# Revit family: Elevator_10913
name_source: partatom
category: Generic Models
revit_build: Autodesk Revit 2016 (Build: 20150714_1515(x64)
units: mm (PartAtom-declared; Revit-internal decimal feet)

## family parameters
Always vertical = Yes
Can host rebar = No
Cut with Voids When Loaded = No
Host = Wall
Part Type = Normal
Room Calculation Point = No
Round Connector Dimension = Use Diameter
Shared = No

## types (8) — shared parameters
Car Offset at Frame_Right = 0.14 m
Car Wall Thickness = 0.03 m
Dimension 03 = 0.03 m
Dimension 04 = 0.11 m
Dimension B = 1.05 m
Dimension L = 0.17 m
Door Thickness = 0.03 m
Frame Offset_Inside = 0.03 m
Frame Width = 0.05 m
Left Lobby Door Offset = 0.03 m
Weight Capacity Type Information = 1=2000 / 2=2500 / 3=3000 / 4=3500 / 5=4000 / 6=4500 / 7=5000 / 8=6000 / 9=10,000 / 10=12,000
_Elevator Door Height = 2.13 m
_Elevator Pit Depth = 1.22 m

## per-type parameters (varying)
- Service / Hospital_4000: CDI Car Inside=2.26 m; CWI Car Inside=1.73 m; CWI Car Inside Left=1.04 m; CWI Car Inside Right=0.69 m; CWI Car Inside_Half=0.86 m; Car Offset From Wall=0.27 m; Car Offset at Frame_Left=0.1 m; Centerline of Car Opening=1.61 m; Centerline of Opening=1.61 m; Clear Opening=1.22 m; Clear Opening_Half=0.61 m; Dimension 02=0.14 m; Dimension F=1.39 m; Dimension K=1.25 m; HD CL Hoistway and Pit=2.79 m; HW Clear Hoistway and Pit=2.54 m; Head and Sill_Left of Center=1.37 m; Head and Sill_Right of Center=0.71 m; Horizontal Location of Left Door=1.64 m; Horizontal Location of Right Door=1.59 m; Left Elevator Door Offset=0.27 m; Left Elevator Door Width=0.69 m; Rail Layout 01=Yes; Rail Layout 02=No; Right Elevator Door Offset=0.23 m; Right Elevator Door Width=0.69 m; Right Lobby Door Offset=0.07 m; Sill Width=0.11 m; WC=4000; Weight Capacity Type=5; _Elevator Car Inside Width Dimension=1.73 m; _Elevator Clear Hoistway Depth=2.79 m; _Elevator Clear Hoistway Width=2.54 m; _Elevator Clear Opening Dimension=1.22 m; _Elevator Interior Car Depth=2.26 m; _Elevator Weight Capacity=4000
- Service / Hospital_4500: CDI Car Inside=2.41 m; CWI Car Inside=1.73 m; CWI Car Inside Left=1.04 m; CWI Car Inside Right=0.69 m; CWI Car Inside_Half=0.86 m; Car Offset From Wall=0.27 m; Car Offset at Frame_Left=0.1 m; Centerline of Car Opening=1.61 m; Centerline of Opening=1.61 m; Clear Opening=1.22 m; Clear Opening_Half=0.61 m; Dimension 02=0.14 m; Dimension F=1.46 m; Dimension K=1.25 m; HD CL Hoistway and Pit=2.95 m; HW Clear Hoistway and Pit=2.54 m; Head and Sill_Left of Center=1.37 m; Head and Sill_Right of Center=0.71 m; Horizontal Location of Left Door=1.64 m; Horizontal Location of Right Door=1.59 m; Left Elevator Door Offset=0.27 m; Left Elevator Door Width=0.69 m; Rail Layout 01=Yes; Rail Layout 02=No; Right Elevator Door Offset=0.23 m; Right Elevator Door Width=0.69 m; Right Lobby Door Offset=0.07 m; Sill Width=0.11 m; WC=4500; Weight Capacity Type=6; _Elevator Car Inside Width Dimension=1.73 m; _Elevator Clear Hoistway Depth=2.95 m; _Elevator Clear Hoistway Width=2.54 m; _Elevator Clear Opening Dimension=1.22 m; _Elevator Interior Car Depth=2.41 m; _Elevator Weight Capacity=4500
- Service / Hospital_5000: CDI Car Inside=2.59 m; CWI Car Inside=1.8 m; CWI Car Inside Left=1.04 m; CWI Car Inside Right=0.76 m; CWI Car Inside_Half=0.9 m; Car Offset From Wall=0.27 m; Car Offset at Frame_Left=0.1 m; Centerline of Car Opening=1.61 m; Centerline of Opening=1.61 m; Clear Opening=1.37 m; Clear Opening_Half=0.69 m; Dimension 02=0.14 m; Dimension F=1.55 m; Dimension K=1.28 m; HD CL Hoistway and Pit=3.12 m; HW Clear Hoistway and Pit=2.62 m; Head and Sill_Left of Center=1.47 m; Head and Sill_Right of Center=0.79 m; Horizontal Location of Left Door=1.64 m; Horizontal Location of Right Door=1.59 m; Left Elevator Door Offset=0.27 m; Left Elevator Door Width=0.76 m; Rail Layout 01=Yes; Rail Layout 02=No; Right Elevator Door Offset=0.23 m; Right Elevator Door Width=0.76 m; Right Lobby Door Offset=0.07 m; Sill Width=0.11 m; WC=5000; Weight Capacity Type=7; _Elevator Car Inside Width Dimension=1.8 m; _Elevator Clear Hoistway Depth=3.12 m; _Elevator Clear Hoistway Width=2.62 m; _Elevator Clear Opening Dimension=1.37 m; _Elevator Interior Car Depth=2.59 m; _Elevator Weight Capacity=5000
- Passenger_2000: CDI Car Inside=1.3 m; CWI Car Inside=1.75 m; CWI Car Inside Left=1.26 m; CWI Car Inside Right=0.48 m; CWI Car Inside_Half=0.87 m; Car Offset From Wall=0.21 m; Car Offset at Frame_Left=0.14 m; Centerline of Car Opening=1.53 m; Centerline of Opening=1.53 m; Clear Opening=0.91 m; Clear Opening_Half=0.46 m; Dimension 02=0.13 m; Dimension F=0.87 m; Dimension K=1.25 m; HD CL Hoistway and Pit=2.11 m; HW Clear Hoistway and Pit=2.29 m; Head and Sill_Left of Center=1.45 m; Head and Sill_Right of Center=0.64 m; Horizontal Location of Left Door=2.04 m; Horizontal Location of Right Door=1.03 m; Left Elevator Door Offset=0.17 m; Left Elevator Door Width=1.02 m; Rail Layout 01=No; Rail Layout 02=Yes; Right Elevator Door Offset=0.17 m; Right Elevator Door Width=1.02 m; Right Lobby Door Offset=0.03 m; Sill Width=0.13 m; WC=2000; Weight Capacity Type=1; _Elevator Car Inside Width Dimension=1.75 m; _Elevator Clear Hoistway Depth=2.11 m; _Elevator Clear Hoistway Width=2.29 m; _Elevator Clear Opening Dimension=0.91 m; _Elevator Interior Car Depth=1.3 m; _Elevator Weight Capacity=2000
- Passenger_2500: CDI Car Inside=1.3 m; CWI Car Inside=2.03 m; CWI Car Inside Left=1.02 m; CWI Car Inside Right=1.02 m; CWI Car Inside_Half=1.02 m; Car Offset From Wall=0.21 m; Car Offset at Frame_Left=0.14 m; Centerline of Car Opening=1.3 m; Centerline of Opening=1.3 m; Clear Opening=1.07 m; Clear Opening_Half=0.53 m; Dimension 02=0.13 m; Dimension F=0.87 m; Dimension K=1.25 m; HD CL Hoistway and Pit=2.11 m; HW Clear Hoistway and Pit=2.59 m; Head and Sill_Left of Center=1.12 m; Head and Sill_Right of Center=1.12 m; Horizontal Location of Left Door=1.3 m; Horizontal Location of Right Door=1.3 m; Left Elevator Door Offset=0.17 m; Left Elevator Door Width=0.58 m; Rail Layout 01=No; Rail Layout 02=Yes; Right Elevator Door Offset=0.17 m; Right Elevator Door Width=0.58 m; Right Lobby Door Offset=0.03 m; Sill Width=0.13 m; WC=2500; Weight Capacity Type=2; _Elevator Car Inside Width Dimension=2.03 m; _Elevator Clear Hoistway Depth=2.11 m; _Elevator Clear Hoistway Width=2.59 m; _Elevator Clear Opening Dimension=1.07 m; _Elevator Interior Car Depth=1.3 m; _Elevator Weight Capacity=2500
- Passenger_3000: CDI Car Inside=1.45 m; CWI Car Inside=2.03 m; CWI Car Inside Left=1.02 m; CWI Car Inside Right=1.02 m; CWI Car Inside_Half=1.02 m; Car Offset From Wall=0.21 m; Car Offset at Frame_Left=0.14 m; Centerline of Car Opening=1.3 m; Centerline of Opening=1.3 m; Clear Opening=1.07 m; Clear Opening_Half=0.53 m; Dimension 02=0.13 m; Dimension F=1.05 m; Dimension K=1.25 m; HD CL Hoistway and Pit=2.2 m; HW Clear Hoistway and Pit=2.59 m; Head and Sill_Left of Center=1.12 m; Head and Sill_Right of Center=1.12 m; Horizontal Location of Left Door=1.3 m; Horizontal Location of Right Door=1.3 m; Left Elevator Door Offset=0.17 m; Left Elevator Door Width=0.58 m; Rail Layout 01=No; Rail Layout 02=Yes; Right Elevator Door Offset=0.17 m; Right Elevator Door Width=0.58 m; Right Lobby Door Offset=0.03 m; Sill Width=0.13 m; WC=3000; Weight Capacity Type=3; _Elevator Car Inside Width Dimension=2.03 m; _Elevator Clear Hoistway Depth=2.2 m; _Elevator Clear Hoistway Width=2.59 m; _Elevator Clear Opening Dimension=1.07 m; _Elevator Interior Car Depth=1.45 m; _Elevator Weight Capacity=3000
- Passenger_3500: CDI Car Inside=1.65 m; CWI Car Inside=2.03 m; CWI Car Inside Left=1.02 m; CWI Car Inside Right=1.02 m; CWI Car Inside_Half=1.02 m; Car Offset From Wall=0.21 m; Car Offset at Frame_Left=0.14 m; Centerline of Car Opening=1.3 m; Centerline of Opening=1.3 m; Clear Opening=1.07 m; Clear Opening_Half=0.53 m; Dimension 02=0.13 m; Dimension F=0.95 m; Dimension K=1.25 m; HD CL Hoistway and Pit=2.41 m; HW Clear Hoistway and Pit=2.59 m; Head and Sill_Left of Center=1.12 m; Head and Sill_Right of Center=1.12 m; Horizontal Location of Left Door=1.3 m; Horizontal Location of Right Door=1.3 m; Left Elevator Door Offset=0.17 m; Left Elevator Door Width=0.58 m; Rail Layout 01=No; Rail Layout 02=Yes; Right Elevator Door Offset=0.17 m; Right Elevator Door Width=0.58 m; Right Lobby Door Offset=0.03 m; Sill Width=0.13 m; WC=3500; Weight Capacity Type=4; _Elevator Car Inside Width Dimension=2.03 m; _Elevator Clear Hoistway Depth=2.41 m; _Elevator Clear Hoistway Width=2.59 m; _Elevator Clear Opening Dimension=1.07 m; _Elevator Interior Car Depth=1.65 m; _Elevator Weight Capacity=3500
- Passenger_4000: CDI Car Inside=1.65 m; CWI Car Inside=2.34 m; CWI Car Inside Left=1.17 m; CWI Car Inside Right=1.17 m; CWI Car Inside_Half=1.17 m; Car Offset From Wall=0.21 m; Car Offset at Frame_Left=0.14 m; Centerline of Car Opening=1.45 m; Centerline of Opening=1.45 m; Clear Opening=1.22 m; Clear Opening_Half=0.61 m; Dimension 02=0.13 m; Dimension F=1.05 m; Dimension K=1.25 m; HD CL Hoistway and Pit=2.41 m; HW Clear Hoistway and Pit=2.9 m; Head and Sill_Left of Center=1.27 m; Head and Sill_Right of Center=1.27 m; Horizontal Location of Left Door=1.45 m; Horizontal Location of Right Door=1.45 m; Left Elevator Door Offset=0.17 m; Left Elevator Door Width=0.66 m; Rail Layout 01=No; Rail Layout 02=Yes; Right Elevator Door Offset=0.17 m; Right Elevator Door Width=0.66 m; Right Lobby Door Offset=0.03 m; Sill Width=0.13 m; WC=4000; Weight Capacity Type=5; _Elevator Car Inside Width Dimension=2.34 m; _Elevator Clear Hoistway Depth=2.41 m; _Elevator Clear Hoistway Width=2.9 m; _Elevator Clear Opening Dimension=1.22 m; _Elevator Interior Car Depth=1.65 m; _Elevator Weight Capacity=4000

## geometry (parser evidence)
native form markers: Sweep x15
no freeform markers — native parametric forms only
